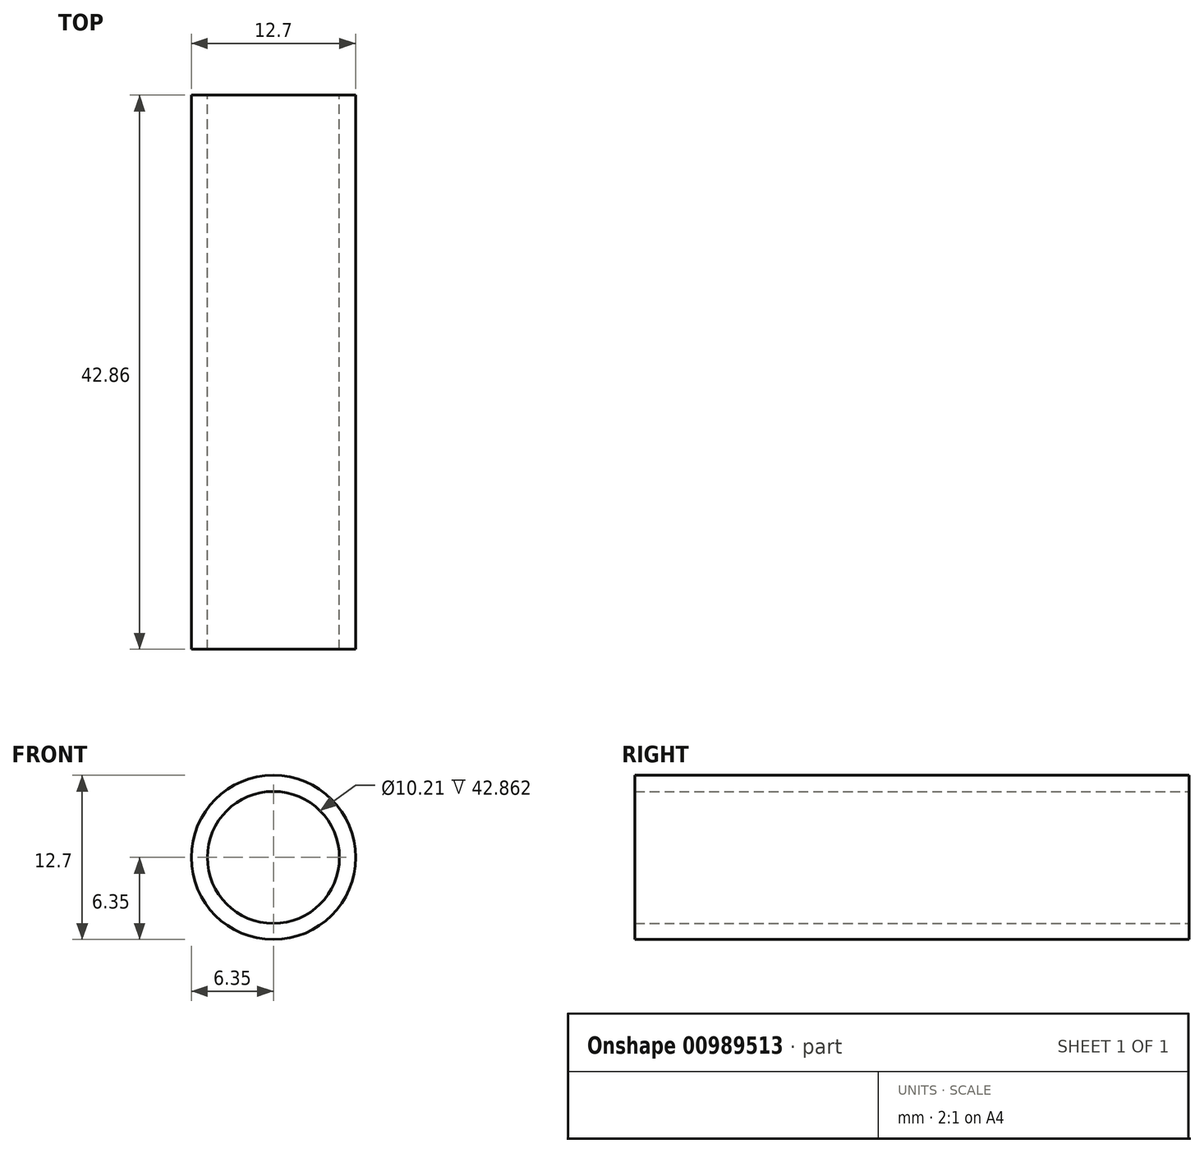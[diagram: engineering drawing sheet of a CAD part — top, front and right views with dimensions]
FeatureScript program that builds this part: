
annotation { "Feature Type Name" : "Feature", "Feature Type Description" : "" }
export const myFeature = defineFeature(function(context is Context, id is Id, definition is map)
    precondition{}
    {
        {
            var Q0;
            Q0=qCreatedBy(makeId("Front.planeOp"),FACE);
            var sketch = newSketch(context, id + "F0", { "sketchPlane" : qUnion([Q0])});
            skCircle(sketch, "E0", {"center": v(0, 0) * mm, "radius": 6.35 * mm});
            skCircle(sketch, "E1", {"center": v(0, 0) * mm, "radius": 5.1 * mm});
            skSolve(sketch);
        }
        {
            var Q0;
            Q0 = qSketchRegion(id + "F0", true);
            extrude(context, id + "F1", {"entities" : qUnion([Q0]), "depth" : 42.86 * mm, "offsetDistance" : 25.4 * mm});
        }
    });
